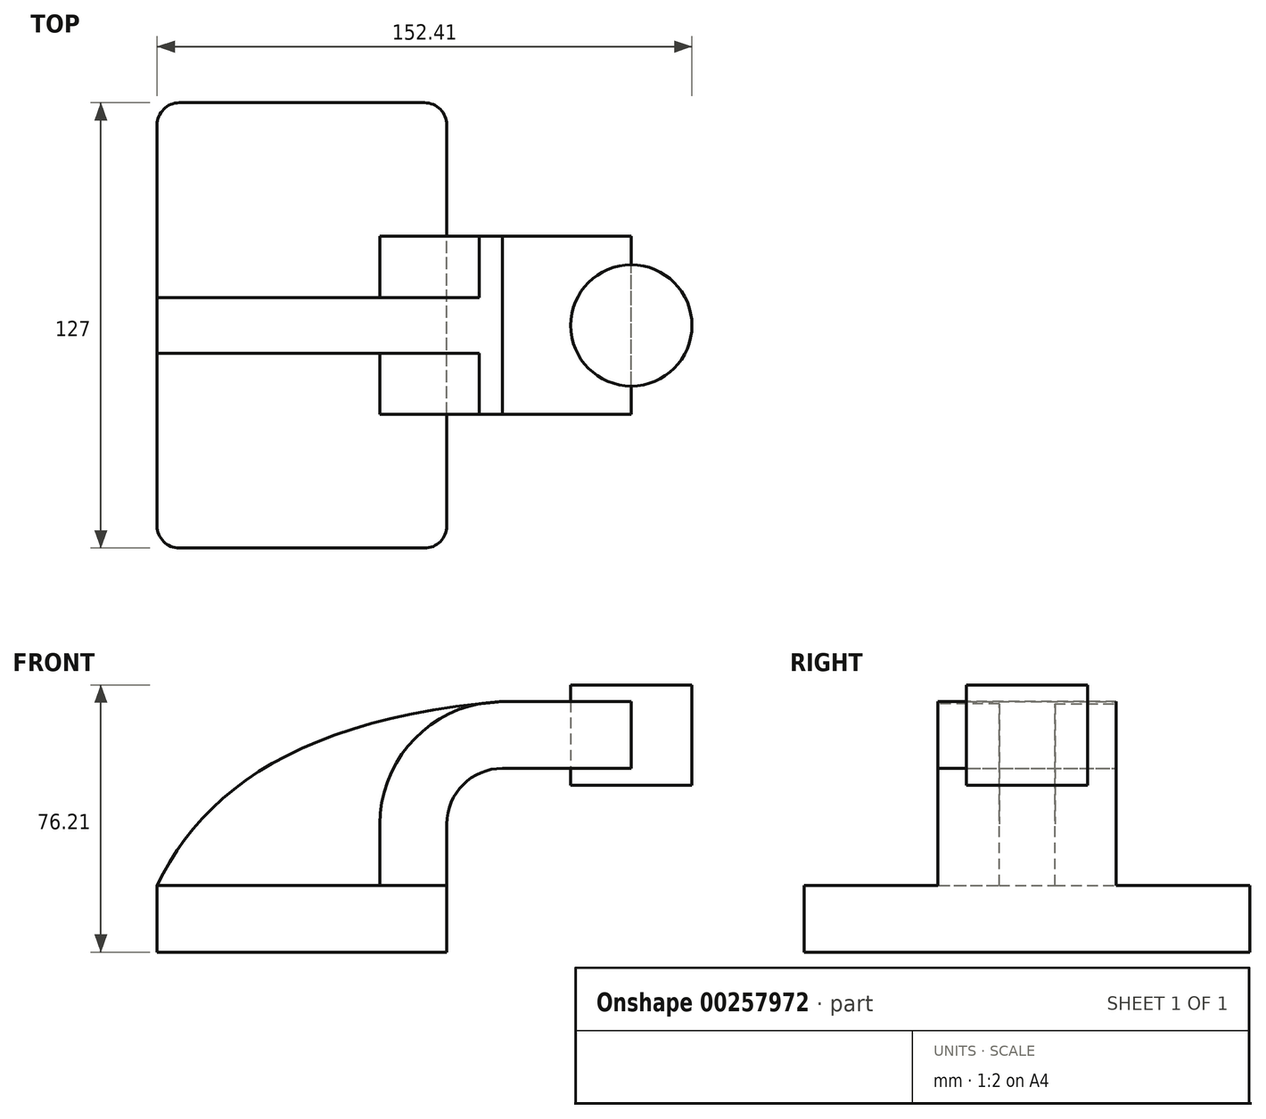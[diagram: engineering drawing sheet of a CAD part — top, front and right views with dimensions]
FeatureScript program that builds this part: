
annotation { "Feature Type Name" : "Feature", "Feature Type Description" : "" }
export const myFeature = defineFeature(function(context is Context, id is Id, definition is map)
    precondition{}
    {
        {
            var Q0;
            Q0=qCreatedBy(makeId("Front.planeOp"),FACE);
            var sketch = newSketch(context, id + "F0", { "sketchPlane" : qUnion([Q0])});
            skLineSegment(sketch, "E0.bottom", {"start": v(-41.28, 9.52) * mm, "end": v(41.27, 9.53) * mm});
            skLineSegment(sketch, "E0.top", {"start": v(-41.27, -9.53) * mm, "end": v(41.28, -9.53) * mm});
            skLineSegment(sketch, "E0.left", {"start": v(-41.28, 9.52) * mm, "end": v(-41.27, -9.53) * mm});
            skLineSegment(sketch, "E0.right", {"start": v(41.28, 9.53) * mm, "end": v(41.28, -9.52) * mm});
            skPoint(sketch, "E0.middle", {"position": v(0, 0) * mm});
            skLineSegment(sketch, "E1.bottom", {"start": v(60.32, 66.68) * mm, "end": v(111.12, 66.68) * mm});
            skLineSegment(sketch, "E1.top", {"start": v(60.32, 38.1) * mm, "end": v(111.12, 38.1) * mm});
            skLineSegment(sketch, "E1.left", {"start": v(60.32, 66.67) * mm, "end": v(60.32, 38.1) * mm});
            skLineSegment(sketch, "E1.right", {"start": v(111.12, 66.67) * mm, "end": v(111.12, 38.1) * mm});
            skPoint(sketch, "E1.middle", {"position": v(85.72, 52.39) * mm});
            skLineSegment(sketch, "E2", {"start": v(41.27, 9.53) * mm, "end": v(41.27, 27) * mm});
            skArc(sketch, "E3", {"start": v(41.27, 27) * mm, "mid": v(45.92, 38.23) * mm, "end": v(57.15, 42.88) * mm});
            skLineSegment(sketch, "E4", {"start": v(57.15, 42.88) * mm, "end": v(93.84, 42.88) * mm});
            skLineSegment(sketch, "E5.0", {"start": v(57.15, 61.93) * mm, "end": v(93.84, 61.93) * mm});
            skArc(sketch, "E5.1", {"start": v(22.22, 27) * mm, "mid": v(32.45, 51.7) * mm, "end": v(57.15, 61.93) * mm});
            skLineSegment(sketch, "E5.2", {"start": v(22.22, 9.53) * mm, "end": v(22.22, 27) * mm});
            skLineSegment(sketch, "E6", {"start": v(93.84, 38.1) * mm, "end": v(93.84, 61.93) * mm});
            skLineSegment(sketch, "E7", {"start": v(93.84, 61.93) * mm, "end": v(93.84, 66.68) * mm});
            skFitSpline(sketch, "E8", {"points": [v(-41.28, 9.52) * mm, v(57.15, 61.93) * mm], "startDerivative": vector(39.2, 82.01) * mm, "endDerivative": vector(171.45, 14.24) * mm});
            skSolve(sketch);
        }
        {
            var Q0;
            Q0=makeQuery(id+"F0.imprint","IMPRINT",FACE,{"disambiguationData":[TD([[makeQuery(id+"F0.imprint","IMPRINT",EDGE,{"derivedFrom":sQuery(id+"F0.wireOp",EDGE,"E0.top")}),1.0]])]});
            extrude(context, id + "F1", {"entities" : qUnion([Q0]), "endBound" : BoundingType.SYMMETRIC, "depth" : 127 * mm});
        }
        {
            var Q0;
            {var subQ0=sQuery(id+"F0.wireOp",EDGE,"E5.0");var subQ1=sQuery(id+"F0.wireOp",EDGE,"E1.left");var subQ2=makeQuery(id+"F0.imprint","INTERSECT",VERTEX,{"derivedFrom":[subQ1,subQ0]});Q0=makeQuery(id+"F0.imprint","IMPRINT",FACE,{"disambiguationData":[TD([[makeQuery(id+"F0.imprint","IMPRINT",EDGE,{"disambiguationData":[TD([[subQ2,-1.0]])],"derivedFrom":subQ1}),1.0]])]});}
            var Q1;
            {var subQ1=sQuery(id+"F0.wireOp",EDGE,"E2");Q1=makeQuery(id+"F0.imprint","IMPRINT",FACE,{"disambiguationData":[TD([[makeQuery(id+"F0.imprint","IMPRINT",EDGE,{"derivedFrom":subQ1}),1.0]])]});}
            extrude(context, id + "F2", {"entities" : qUnion([Q0, Q1]), "operationType" : NewBodyOperationType.ADD, "endBound" : BoundingType.SYMMETRIC, "depth" : 50.8 * mm});
        }
        {
            var Q0;
            {var subQ3=sQuery(id+"F0.wireOp",EDGE,"E5.2");Q0=makeQuery(id+"F0.imprint","IMPRINT",FACE,{"disambiguationData":[TD([[makeQuery(id+"F0.imprint","IMPRINT",EDGE,{"derivedFrom":subQ3}),1.0]])]});}
            extrude(context, id + "F3", {"entities" : qUnion([Q0]), "operationType" : NewBodyOperationType.ADD, "endBound" : BoundingType.SYMMETRIC, "depth" : 15.88 * mm});
        }
        {
            var Q0;
            {var subQ0=sQuery(id+"F0.wireOp",EDGE,"E1.right");Q0=makeQuery(id+"F0.imprint","IMPRINT",FACE,{"disambiguationData":[TD([[makeQuery(id+"F0.imprint","IMPRINT",EDGE,{"derivedFrom":subQ0}),-1.0]])]});}
            var Q1;
            Q1=sQuery(id+"F0.wireOp",EDGE,"E7");
            revolve(context, id + "F4", {"entities" : qUnion([Q0]), "axis" : qUnion([Q1]), "revolveType" : RevolveType.FULL});
        }
        {
            var Q0;
            Q0=makeQuery(id+"F1.opExtrude","CAP_EDGE",EDGE,{"disambiguationData":[OSD([sQuery(id+"F0.wireOp",EDGE,"E0.left")])],"isStart":false});
            var Q1;
            Q1=makeQuery(id+"F1.opExtrude","CAP_EDGE",EDGE,{"disambiguationData":[OSD([sQuery(id+"F0.wireOp",EDGE,"E0.right")])],"isStart":false});
            var Q2;
            Q2=makeQuery(id+"F1.opExtrude","CAP_EDGE",EDGE,{"disambiguationData":[OSD([sQuery(id+"F0.wireOp",EDGE,"E0.right")])],"isStart":true});
            var Q3;
            Q3=makeQuery(id+"F1.opExtrude","CAP_EDGE",EDGE,{"disambiguationData":[OSD([sQuery(id+"F0.wireOp",EDGE,"E0.left")])],"isStart":true});
            fillet(context, id + "F5", {"entities" : qUnion([Q0, Q1, Q2, Q3]), "radius" : 6.35 * mm, "tangentPropagation" : true, "allowEdgeOverflow" : false});
        }
    });
